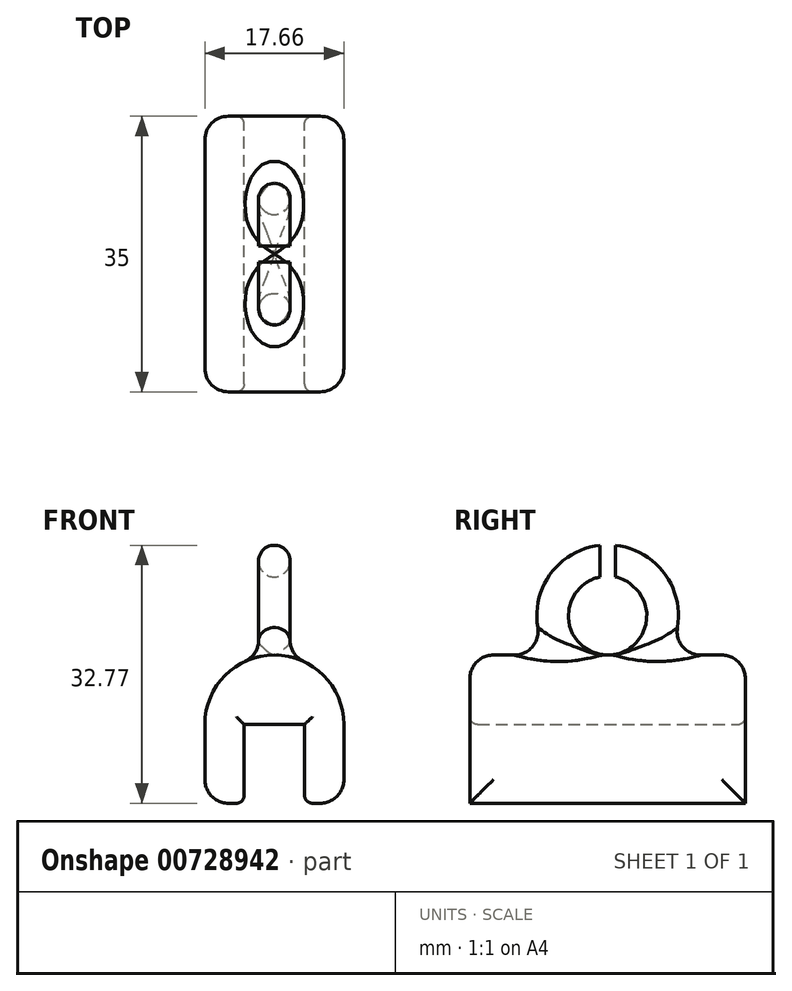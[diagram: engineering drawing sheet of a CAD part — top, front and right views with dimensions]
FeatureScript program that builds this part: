
annotation { "Feature Type Name" : "Feature", "Feature Type Description" : "" }
export const myFeature = defineFeature(function(context is Context, id is Id, definition is map)
    precondition{}
    {
        {
            var Q0;
            Q0=qCreatedBy(makeId("Front.planeOp"),FACE);
            var sketch = newSketch(context, id + "F0", { "sketchPlane" : qUnion([Q0])});
            skLineSegment(sketch, "E0", {"start": v(-3.83, 0) * mm, "end": v(3.83, 0) * mm});
            skLineSegment(sketch, "E1", {"start": v(3.83, 0) * mm, "end": v(3.83, -10) * mm});
            skLineSegment(sketch, "E2", {"start": v(3.83, -10) * mm, "end": v(8.83, -10) * mm});
            skLineSegment(sketch, "E3", {"start": v(8.83, -10) * mm, "end": v(8.83, 0) * mm});
            skLineSegment(sketch, "E4", {"start": v(-8.83, 0) * mm, "end": v(-8.83, -10) * mm});
            skLineSegment(sketch, "E5", {"start": v(-8.83, -10) * mm, "end": v(-3.83, -10) * mm});
            skLineSegment(sketch, "E6", {"start": v(-3.83, -10) * mm, "end": v(-3.83, 0) * mm});
            skArc(sketch, "E7", {"start": v(8.83, 0) * mm, "mid": v(0, 8.83) * mm, "end": v(-8.83, 0) * mm});
            skSolve(sketch);
        }
        {
            var Q0;
            Q0=qCreatedBy(makeId("Front.planeOp"),FACE);
            var sketch = newSketch(context, id + "F1", { "sketchPlane" : qUnion([Q0])});
            skCircle(sketch, "E8", {"center": v(0, 6.83) * mm, "radius": 2 * mm});
            skPoint(sketch, "E9", {"position": v(0, 8.83) * mm});
            skSolve(sketch);
        }
        {
            var Q0;
            Q0 = qSketchRegion(id + "F0", true);
            extrude(context, id + "F2", {"entities" : qUnion([Q0]), "endBound" : BoundingType.SYMMETRIC, "depth" : 35 * mm, "offsetDistance" : 25 * mm});
        }
        {
            var Q0;
            Q0=qCreatedBy(makeId("Right.planeOp"),FACE);
            var sketch = newSketch(context, id + "F3", { "sketchPlane" : qUnion([Q0])});
            skCircle(sketch, "E10", {"center": v(0, 13.83) * mm, "radius": 5 * mm});
            skPoint(sketch, "E11", {"position": v(0, 8.83) * mm});
            skSolve(sketch);
        }
        {
            var Q0;
            Q0 = qSketchRegion(id + "F1", true);
            var Q1;
            Q1=sQuery(id+"F3.wireOp",EDGE,"E10");
            sweep(context, id + "F4", {"operationType" : NewBodyOperationType.ADD, "profiles" : qUnion([Q0]), "path" : qUnion([Q1])});
        }
        {
            var Q0;
            Q0=qCreatedBy(makeId("Right.planeOp"),FACE);
            var sketch = newSketch(context, id + "F5", { "sketchPlane" : qUnion([Q0])});
            skLineSegment(sketch, "E12.bottom", {"start": v(-1, 13.83) * mm, "end": v(1, 13.83) * mm});
            skLineSegment(sketch, "E12.top", {"start": v(-1, 23.83) * mm, "end": v(1, 23.83) * mm});
            skLineSegment(sketch, "E12.left", {"start": v(-1, 13.83) * mm, "end": v(-1, 23.83) * mm});
            skLineSegment(sketch, "E12.right", {"start": v(1, 13.83) * mm, "end": v(1, 23.83) * mm});
            skPoint(sketch, "E12.middle", {"position": v(0, 18.83) * mm});
            skSolve(sketch);
        }
        {
            var Q0;
            Q0 = qSketchRegion(id + "F5", true);
            extrude(context, id + "F6", {"entities" : qUnion([Q0]), "operationType" : NewBodyOperationType.REMOVE, "endBound" : BoundingType.SYMMETRIC, "oppositeDirection" : true, "depth" : 5 * mm, "offsetDistance" : 25 * mm});
        }
        {
            var Q0;
            Q0=makeQuery(id+"F2.opExtrude","CAP_EDGE",EDGE,{"disambiguationData":[OSD([sQuery(id+"F0.wireOp",EDGE,"E4")])],"isStart":true});
            var Q1;
            Q1=makeQuery(id+"F2.opExtrude","CAP_EDGE",EDGE,{"disambiguationData":[OSD([sQuery(id+"F0.wireOp",EDGE,"E4")])],"isStart":false});
            var Q2;
            Q2=makeQuery(id+"F2.opExtrude","SWEPT_EDGE",EDGE,{"disambiguationData":[OSD([sQuery(id+"F0.wireOp",EDGE,"E4"),sQuery(id+"F0.wireOp",EDGE,"E5")])]});
            var Q3;
            Q3=makeQuery(id+"F2.opExtrude","SWEPT_EDGE",EDGE,{"disambiguationData":[OSD([sQuery(id+"F0.wireOp",EDGE,"E2"),sQuery(id+"F0.wireOp",EDGE,"E3")])]});
            fillet(context, id + "F7", {"entities" : qUnion([Q0, Q1, Q2, Q3]), "radius" : 3 * mm, "tangentPropagation" : true, "allowEdgeOverflow" : false});
        }
        {
            var Q0;
            Q0=makeQuery(id+"F2.opExtrude","SWEPT_EDGE",EDGE,{"disambiguationData":[OSD([sQuery(id+"F0.wireOp",EDGE,"E1"),sQuery(id+"F0.wireOp",EDGE,"E2")])]});
            var Q1;
            Q1=makeQuery(id+"F2.opExtrude","CAP_EDGE",EDGE,{"disambiguationData":[OSD([sQuery(id+"F0.wireOp",EDGE,"E1")])],"isStart":true});
            var Q2;
            Q2=makeQuery(id+"F2.opExtrude","CAP_EDGE",EDGE,{"disambiguationData":[OSD([sQuery(id+"F0.wireOp",EDGE,"E0")])],"isStart":true});
            var Q3;
            Q3=makeQuery(id+"F2.opExtrude","CAP_EDGE",EDGE,{"disambiguationData":[OSD([sQuery(id+"F0.wireOp",EDGE,"E6")])],"isStart":true});
            var Q4;
            Q4=makeQuery(id+"F2.opExtrude","SWEPT_EDGE",EDGE,{"disambiguationData":[OSD([sQuery(id+"F0.wireOp",EDGE,"E5"),sQuery(id+"F0.wireOp",EDGE,"E6")])]});
            var Q5;
            Q5=makeQuery(id+"F2.opExtrude","CAP_EDGE",EDGE,{"disambiguationData":[OSD([sQuery(id+"F0.wireOp",EDGE,"E6")])],"isStart":false});
            var Q6;
            Q6=makeQuery(id+"F2.opExtrude","CAP_EDGE",EDGE,{"disambiguationData":[OSD([sQuery(id+"F0.wireOp",EDGE,"E0")])],"isStart":false});
            var Q7;
            Q7=makeQuery(id+"F2.opExtrude","CAP_EDGE",EDGE,{"disambiguationData":[OSD([sQuery(id+"F0.wireOp",EDGE,"E1")])],"isStart":false});
            fillet(context, id + "F8", {"entities" : qUnion([Q0, Q1, Q2, Q3, Q4, Q5, Q6, Q7]), "radius" : 1 * mm, "tangentPropagation" : true, "allowEdgeOverflow" : false});
        }
        {
            var Q0;
            Q0=makeQuery(id+"F4.boolean.opBoolean","INTERSECT",EDGE,{"disambiguationData":[OD(0.0)],"derivedFrom":[makeQuery(id+"F2.opExtrude","SWEPT_FACE",FACE,{"disambiguationData":[OSD([sQuery(id+"F0.wireOp",EDGE,"E7")])]}),makeQuery(id+"F4.opSweep","SWEPT_FACE",FACE,{"disambiguationData":[OSD([sQuery(id+"F1.wireOp",EDGE,"E8"),sQuery(id+"F3.wireOp",EDGE,"E10")])]})]});
            var Q1;
            Q1=makeQuery(id+"F4.boolean.opBoolean","INTERSECT",EDGE,{"disambiguationData":[OD(1.0)],"derivedFrom":[makeQuery(id+"F2.opExtrude","SWEPT_FACE",FACE,{"disambiguationData":[OSD([sQuery(id+"F0.wireOp",EDGE,"E7")])]}),makeQuery(id+"F4.opSweep","SWEPT_FACE",FACE,{"disambiguationData":[OSD([sQuery(id+"F1.wireOp",EDGE,"E8"),sQuery(id+"F3.wireOp",EDGE,"E10")])]})]});
            fillet(context, id + "F9", {"entities" : qUnion([Q0, Q1]), "radius" : 3 * mm, "tangentPropagation" : true, "allowEdgeOverflow" : false});
        }
    });
